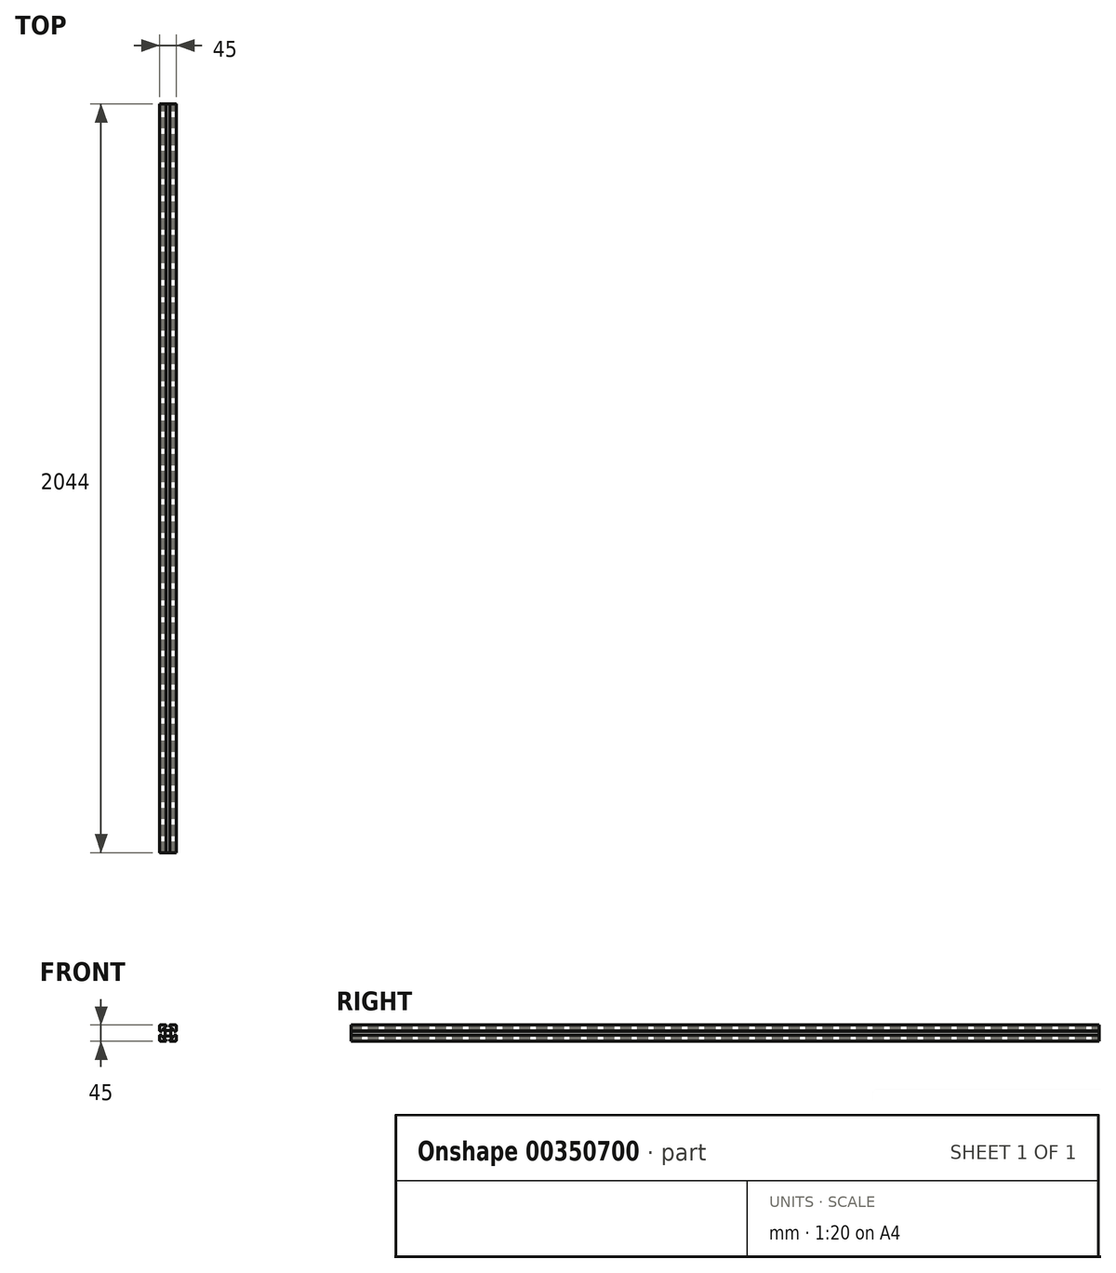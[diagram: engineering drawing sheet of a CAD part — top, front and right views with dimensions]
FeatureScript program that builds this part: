
annotation { "Feature Type Name" : "Feature", "Feature Type Description" : "" }
export const myFeature = defineFeature(function(context is Context, id is Id, definition is map)
    precondition{}
    {
        {
            var Q0;
            Q0=qCreatedBy(makeId("Front.planeOp"),FACE);
            var sketch = newSketch(context, id + "F0", { "sketchPlane" : qUnion([Q0])});
            skLineSegment(sketch, "E0", {"start": v(80.5, 122.5) * mm, "end": v(93.5, 122.5) * mm});
            skLineSegment(sketch, "E1", {"start": v(95, 121) * mm, "end": v(95, 116.5) * mm});
            skLineSegment(sketch, "E2", {"start": v(95, 116.5) * mm, "end": v(90, 116.5) * mm});
            skLineSegment(sketch, "E3", {"start": v(90, 116.5) * mm, "end": v(90, 112.5) * mm});
            skLineSegment(sketch, "E4", {"start": v(90, 112.5) * mm, "end": v(95, 107.5) * mm});
            skLineSegment(sketch, "E5", {"start": v(95, 107.5) * mm, "end": v(100, 107.5) * mm});
            skLineSegment(sketch, "E6", {"start": v(95, 121) * mm, "end": v(94.5, 121) * mm});
            skLineSegment(sketch, "E7", {"start": v(94.5, 121) * mm, "end": v(94.5, 121.5) * mm});
            skPoint(sketch, "E8.orphan", {"position": v(95, 122.5) * mm});
            skPoint(sketch, "E9.visualSharp", {"position": v(94.5, 122.5) * mm});
            skArc(sketch, "E9.filletArc", {"start": v(94.5, 121.5) * mm, "mid": v(94.2, 122.2) * mm, "end": v(93.5, 122.5) * mm});
            skPoint(sketch, "E10.visualSharp", {"position": v(77.5, 122.5) * mm});
            skArc(sketch, "E10.filletArc", {"start": v(80.5, 122.5) * mm, "mid": v(79.35, 122.27) * mm, "end": v(78.38, 121.62) * mm});
            skLineSegment(sketch, "E11.4", {"start": v(-7, 19.5) * mm, "end": v(-7, 19.5) * mm});
            skLineSegment(sketch, "E11.11", {"start": v(-19.5, 7) * mm, "end": v(-19.5, 7) * mm});
            skLineSegment(sketch, "E12", {"start": v(77.5, 122.5) * mm, "end": v(100, 100) * mm, "construction": true});
            skLineSegment(sketch, "E13.MirrorCS", {"start": v(92.5, 105) * mm, "end": v(92.5, 100) * mm});
            skLineSegment(sketch, "E14.MirrorCS", {"start": v(87.5, 110) * mm, "end": v(92.5, 105) * mm});
            skLineSegment(sketch, "E15.MirrorCS", {"start": v(83.5, 110) * mm, "end": v(87.5, 110) * mm});
            skLineSegment(sketch, "E16.MirrorCS", {"start": v(83.5, 105) * mm, "end": v(83.5, 110) * mm});
            skLineSegment(sketch, "E17.MirrorCS", {"start": v(79, 105) * mm, "end": v(83.5, 105) * mm});
            skLineSegment(sketch, "E18.MirrorCS", {"start": v(79, 105) * mm, "end": v(79, 105.5) * mm});
            skLineSegment(sketch, "E19.MirrorCS", {"start": v(79, 105.5) * mm, "end": v(78.5, 105.5) * mm});
            skArc(sketch, "E20.MirrorCS", {"start": v(78.5, 105.5) * mm, "mid": v(77.8, 105.8) * mm, "end": v(77.5, 106.5) * mm});
            skLineSegment(sketch, "E21.MirrorCS", {"start": v(77.5, 119.5) * mm, "end": v(77.5, 106.5) * mm});
            skArc(sketch, "E22.MirrorCS", {"start": v(77.5, 119.5) * mm, "mid": v(77.73, 120.65) * mm, "end": v(78.38, 121.62) * mm});
            skLineSegment(sketch, "E23.MirrorCS", {"start": v(105, 121) * mm, "end": v(105.5, 121) * mm});
            skLineSegment(sketch, "E24.MirrorCS", {"start": v(105.5, 121) * mm, "end": v(105.5, 121.5) * mm});
            skLineSegment(sketch, "E25.MirrorCS", {"start": v(121, 105.5) * mm, "end": v(121.5, 105.5) * mm});
            skLineSegment(sketch, "E26.MirrorCS", {"start": v(121, 105) * mm, "end": v(121, 105.5) * mm});
            skArc(sketch, "E27.MirrorCS", {"start": v(105.5, 121.5) * mm, "mid": v(105.8, 122.2) * mm, "end": v(106.5, 122.5) * mm});
            skLineSegment(sketch, "E28.MirrorCS", {"start": v(110, 116.5) * mm, "end": v(110, 112.5) * mm});
            skArc(sketch, "E29.MirrorCS", {"start": v(122.5, 119.5) * mm, "mid": v(122.27, 120.65) * mm, "end": v(121.62, 121.62) * mm});
            skLineSegment(sketch, "E30.MirrorCS", {"start": v(112.5, 110) * mm, "end": v(107.5, 105) * mm});
            skLineSegment(sketch, "E31.MirrorCS", {"start": v(110, 112.5) * mm, "end": v(105, 107.5) * mm});
            skPoint(sketch, "E32.MirrorP", {"position": v(105.5, 122.5) * mm});
            skLineSegment(sketch, "E33.MirrorCS", {"start": v(105, 116.5) * mm, "end": v(110, 116.5) * mm});
            skArc(sketch, "E34.MirrorCS", {"start": v(119.5, 122.5) * mm, "mid": v(120.65, 122.27) * mm, "end": v(121.62, 121.62) * mm});
            skLineSegment(sketch, "E35.MirrorCS", {"start": v(121, 105) * mm, "end": v(116.5, 105) * mm});
            skLineSegment(sketch, "E36.MirrorCS", {"start": v(122.5, 119.5) * mm, "end": v(122.5, 106.5) * mm});
            skArc(sketch, "E37.MirrorCS", {"start": v(121.5, 105.5) * mm, "mid": v(122.2, 105.8) * mm, "end": v(122.5, 106.5) * mm});
            skLineSegment(sketch, "E38.MirrorCS", {"start": v(107.5, 105) * mm, "end": v(107.5, 100) * mm});
            skLineSegment(sketch, "E39.MirrorCS", {"start": v(116.5, 110) * mm, "end": v(112.5, 110) * mm});
            skPoint(sketch, "E40.MirrorP", {"position": v(122.5, 122.5) * mm});
            skLineSegment(sketch, "E41.MirrorCS", {"start": v(122.5, 122.5) * mm, "end": v(100, 100) * mm, "construction": true});
            skLineSegment(sketch, "E42.MirrorCS", {"start": v(105, 121) * mm, "end": v(105, 116.5) * mm});
            skLineSegment(sketch, "E43.MirrorCS", {"start": v(116.5, 105) * mm, "end": v(116.5, 110) * mm});
            skLineSegment(sketch, "E44.MirrorCS", {"start": v(105, 107.5) * mm, "end": v(100, 107.5) * mm});
            skPoint(sketch, "E45.MirrorP", {"position": v(105, 122.5) * mm});
            skLineSegment(sketch, "E46.MirrorCS", {"start": v(119.5, 122.5) * mm, "end": v(106.5, 122.5) * mm});
            skLineSegment(sketch, "E47.MirrorCS", {"start": v(94.5, 79) * mm, "end": v(94.5, 78.5) * mm});
            skLineSegment(sketch, "E48.MirrorCS", {"start": v(79, 95) * mm, "end": v(79, 94.5) * mm});
            skLineSegment(sketch, "E49.MirrorCS", {"start": v(95, 92.5) * mm, "end": v(100, 92.5) * mm});
            skLineSegment(sketch, "E50.MirrorCS", {"start": v(79, 94.5) * mm, "end": v(78.5, 94.5) * mm});
            skLineSegment(sketch, "E51.MirrorCS", {"start": v(95, 79) * mm, "end": v(94.5, 79) * mm});
            skArc(sketch, "E52.MirrorCS", {"start": v(94.5, 78.5) * mm, "mid": v(94.2, 77.8) * mm, "end": v(93.5, 77.5) * mm});
            skLineSegment(sketch, "E53.MirrorCS", {"start": v(77.5, 80.5) * mm, "end": v(77.5, 93.5) * mm});
            skLineSegment(sketch, "E54.MirrorCS", {"start": v(83.5, 90) * mm, "end": v(87.5, 90) * mm});
            skPoint(sketch, "E55.MirrorP", {"position": v(95, 77.5) * mm});
            skLineSegment(sketch, "E56.MirrorCS", {"start": v(90, 83.5) * mm, "end": v(90, 87.5) * mm});
            skArc(sketch, "E57.MirrorCS", {"start": v(78.5, 94.5) * mm, "mid": v(77.8, 94.2) * mm, "end": v(77.5, 93.5) * mm});
            skLineSegment(sketch, "E58.MirrorCS", {"start": v(80.5, 77.5) * mm, "end": v(93.5, 77.5) * mm});
            skPoint(sketch, "E59.MirrorP", {"position": v(77.5, 77.5) * mm});
            skPoint(sketch, "E60.MirrorP", {"position": v(94.5, 77.5) * mm});
            skLineSegment(sketch, "E61.MirrorCS", {"start": v(87.5, 90) * mm, "end": v(92.5, 95) * mm});
            skLineSegment(sketch, "E62.MirrorCS", {"start": v(90, 87.5) * mm, "end": v(95, 92.5) * mm});
            skLineSegment(sketch, "E63.MirrorCS", {"start": v(95, 79) * mm, "end": v(95, 83.5) * mm});
            skLineSegment(sketch, "E64.MirrorCS", {"start": v(77.5, 77.5) * mm, "end": v(100, 100) * mm, "construction": true});
            skArc(sketch, "E65.MirrorCS", {"start": v(80.5, 77.5) * mm, "mid": v(79.35, 77.73) * mm, "end": v(78.38, 78.38) * mm});
            skArc(sketch, "E66.MirrorCS", {"start": v(77.5, 80.5) * mm, "mid": v(77.73, 79.35) * mm, "end": v(78.38, 78.38) * mm});
            skLineSegment(sketch, "E67.MirrorCS", {"start": v(83.5, 95) * mm, "end": v(83.5, 90) * mm});
            skLineSegment(sketch, "E68.MirrorCS", {"start": v(95, 83.5) * mm, "end": v(90, 83.5) * mm});
            skLineSegment(sketch, "E69.MirrorCS", {"start": v(79, 95) * mm, "end": v(83.5, 95) * mm});
            skLineSegment(sketch, "E70.MirrorCS", {"start": v(121, 95) * mm, "end": v(121, 94.5) * mm});
            skLineSegment(sketch, "E71.MirrorCS", {"start": v(105, 79) * mm, "end": v(105.5, 79) * mm});
            skLineSegment(sketch, "E72.MirrorCS", {"start": v(105.5, 79) * mm, "end": v(105.5, 78.5) * mm});
            skLineSegment(sketch, "E73.MirrorCS", {"start": v(121, 94.5) * mm, "end": v(121.5, 94.5) * mm});
            skArc(sketch, "E74.MirrorCS", {"start": v(105.5, 78.5) * mm, "mid": v(105.8, 77.8) * mm, "end": v(106.5, 77.5) * mm});
            skArc(sketch, "E75.MirrorCS", {"start": v(122.5, 80.5) * mm, "mid": v(122.27, 79.35) * mm, "end": v(121.62, 78.38) * mm});
            skLineSegment(sketch, "E76.MirrorCS", {"start": v(121, 95) * mm, "end": v(116.5, 95) * mm});
            skArc(sketch, "E77.MirrorCS", {"start": v(121.5, 94.5) * mm, "mid": v(122.2, 94.2) * mm, "end": v(122.5, 93.5) * mm});
            skLineSegment(sketch, "E78.MirrorCS", {"start": v(116.5, 90) * mm, "end": v(112.5, 90) * mm});
            skPoint(sketch, "E79.MirrorP", {"position": v(105, 77.5) * mm});
            skPoint(sketch, "E80.MirrorP", {"position": v(105.5, 77.5) * mm});
            skLineSegment(sketch, "E81.MirrorCS", {"start": v(105, 83.5) * mm, "end": v(110, 83.5) * mm});
            skPoint(sketch, "E82.MirrorP", {"position": v(122.5, 77.5) * mm});
            skLineSegment(sketch, "E83.MirrorCS", {"start": v(112.5, 90) * mm, "end": v(107.5, 95) * mm});
            skLineSegment(sketch, "E84.MirrorCS", {"start": v(110, 83.5) * mm, "end": v(110, 87.5) * mm});
            skLineSegment(sketch, "E85.MirrorCS", {"start": v(110, 87.5) * mm, "end": v(105, 92.5) * mm});
            skLineSegment(sketch, "E86.MirrorCS", {"start": v(116.5, 95) * mm, "end": v(116.5, 90) * mm});
            skArc(sketch, "E87.MirrorCS", {"start": v(119.5, 77.5) * mm, "mid": v(120.65, 77.73) * mm, "end": v(121.62, 78.38) * mm});
            skLineSegment(sketch, "E88.MirrorCS", {"start": v(119.5, 77.5) * mm, "end": v(106.5, 77.5) * mm});
            skLineSegment(sketch, "E89.MirrorCS", {"start": v(105, 79) * mm, "end": v(105, 83.5) * mm});
            skLineSegment(sketch, "E90.MirrorCS", {"start": v(122.5, 80.5) * mm, "end": v(122.5, 93.5) * mm});
            skLineSegment(sketch, "E91.MirrorCS", {"start": v(107.5, 95) * mm, "end": v(107.5, 100) * mm});
            skLineSegment(sketch, "E92.MirrorCS", {"start": v(105, 92.5) * mm, "end": v(100, 92.5) * mm});
            skLineSegment(sketch, "E93.MirrorCS", {"start": v(92.5, 95) * mm, "end": v(92.5, 100) * mm});
            skSolve(sketch);
        }
        {
            var Q0;
            Q0 = qSketchRegion(id + "F0", true);
            extrude(context, id + "F1", {"entities" : qUnion([Q0]), "depth" : 2044 * mm});
        }
    });
